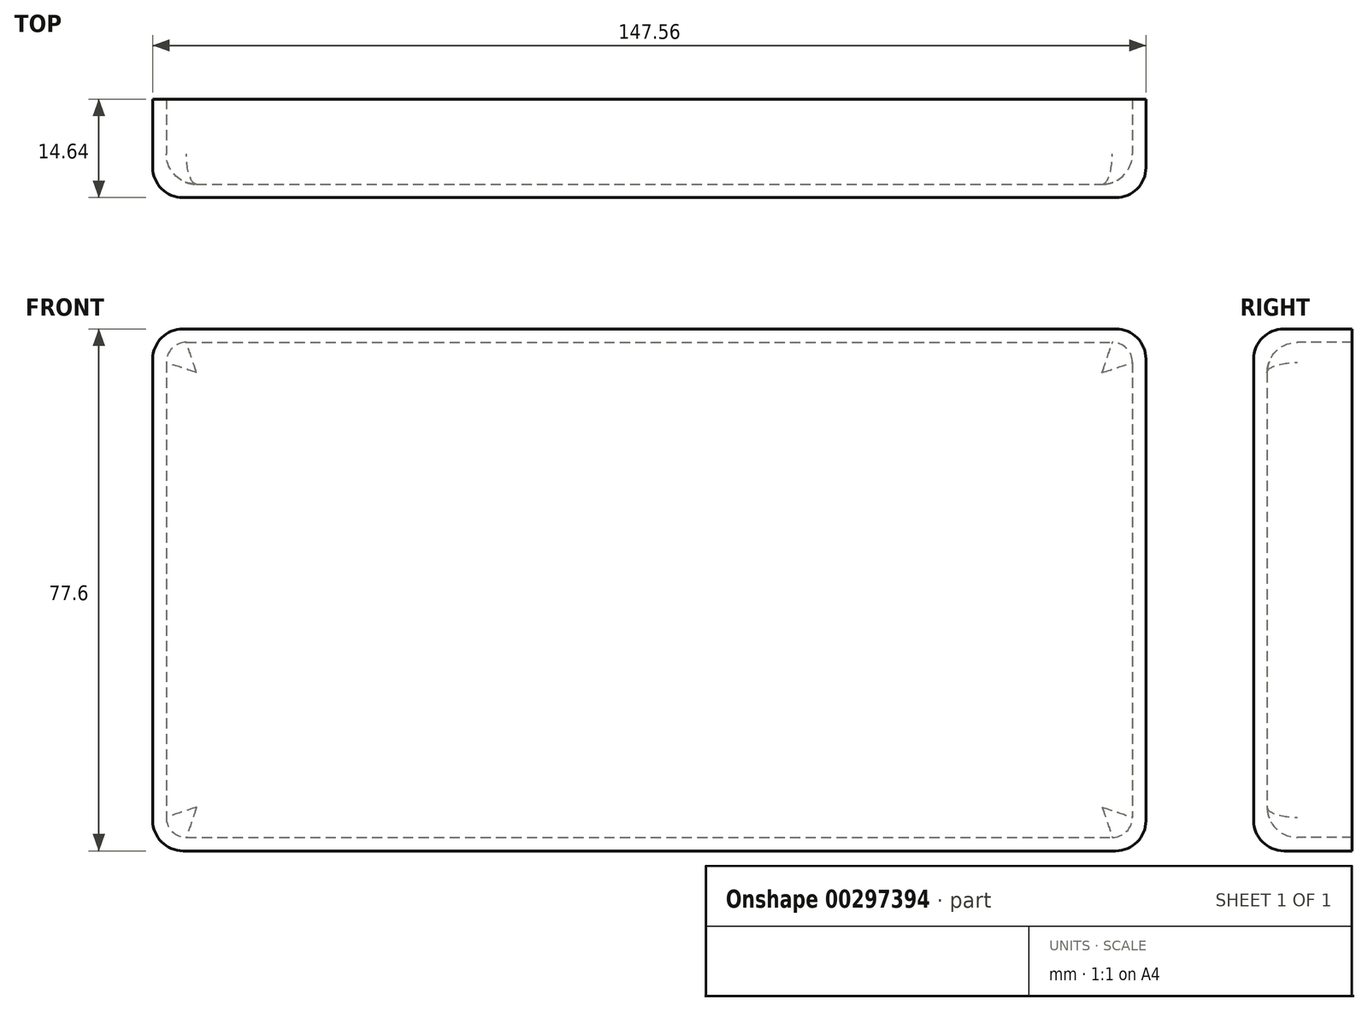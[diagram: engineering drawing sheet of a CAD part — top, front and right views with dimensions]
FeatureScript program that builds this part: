
annotation { "Feature Type Name" : "Feature", "Feature Type Description" : "" }
export const myFeature = defineFeature(function(context is Context, id is Id, definition is map)
    precondition{}
    {
        {
            var Q0;
            Q0=qCreatedBy(makeId("Front.planeOp"),FACE);
            var sketch = newSketch(context, id + "F0", { "sketchPlane" : qUnion([Q0])});
            skLineSegment(sketch, "E0.bottom", {"start": v(-72.06, 43.51) * mm, "end": v(71.5, 43.51) * mm});
            skLineSegment(sketch, "E0.top", {"start": v(-72.06, -30.09) * mm, "end": v(71.5, -30.09) * mm});
            skLineSegment(sketch, "E0.left", {"start": v(-72.06, 43.51) * mm, "end": v(-72.06, -30.09) * mm});
            skLineSegment(sketch, "E0.right", {"start": v(71.5, 43.51) * mm, "end": v(71.5, -30.09) * mm});
            skSolve(sketch);
        }
        {
            var Q0;
            Q0=makeQuery(id+"F0.imprint","IMPRINT",FACE,{"disambiguationData":[TD([[makeQuery(id+"F0.imprint","IMPRINT",EDGE,{"derivedFrom":sQuery(id+"F0.wireOp",EDGE,"E0.bottom")}),-1.0]])]});
            extrude(context, id + "F1", {"entities" : qUnion([Q0]), "oppositeDirection" : true, "depth" : 12.64 * mm});
        }
        {
            var Q0;
            Q0=makeQuery(id+"F1.opExtrude","CAP_FACE",FACE,{"disambiguationData":[OSD([sQuery(id+"F0.wireOp",EDGE,"E0.bottom"),sQuery(id+"F0.wireOp",EDGE,"E0.top"),sQuery(id+"F0.wireOp",EDGE,"E0.left"),sQuery(id+"F0.wireOp",EDGE,"E0.right")])],"isStart":false});
            shell(context, id + "F2", {"entities" : qUnion([Q0]), "thickness" : 2 * mm, "oppositeDirection" : true});
        }
        {
            var Q0;
            Q0=makeQuery(id+"F2.opShell","OFFSET_EDGE",EDGE,{"disambiguationData":[OSD([sQuery(id+"F0.wireOp",EDGE,"E0.top"),sQuery(id+"F0.wireOp",EDGE,"E0.right")])]});
            var Q1;
            Q1=makeQuery(id+"F2.opShell","OFFSET_EDGE",EDGE,{"disambiguationData":[OSD([sQuery(id+"F0.wireOp",EDGE,"E0.bottom"),sQuery(id+"F0.wireOp",EDGE,"E0.right")])]});
            var Q2;
            Q2=makeQuery(id+"F2.opShell","OFFSET_EDGE",EDGE,{"disambiguationData":[OSD([sQuery(id+"F0.wireOp",EDGE,"E0.bottom"),sQuery(id+"F0.wireOp",EDGE,"E0.left")])]});
            var Q3;
            Q3=makeQuery(id+"F2.opShell","OFFSET_EDGE",EDGE,{"disambiguationData":[OSD([sQuery(id+"F0.wireOp",EDGE,"E0.top"),sQuery(id+"F0.wireOp",EDGE,"E0.left")])]});
            fillet(context, id + "F3", {"entities" : qUnion([Q0, Q1, Q2, Q3]), "radius" : 3 * mm, "tangentPropagation" : true, "allowEdgeOverflow" : false});
        }
        {
            var Q0;
            {var subQ0=sQuery(id+"F0.wireOp",EDGE,"E0.right");Q0=makeQuery(id+"F2.opShell","OFFSET_EDGE",EDGE,{"disambiguationData":[OSD([subQ0]),TDD([makeQuery(id+"F1.opExtrude","CAP_EDGE",EDGE,{"disambiguationData":[OSD([subQ0])],"isStart":true})])]});}
            var Q1;
            Q1=makeQuery(id+"F2.opShell","OFFSET_FACE",FACE,{"disambiguationData":[OSD([sQuery(id+"F0.wireOp",EDGE,"E0.bottom"),sQuery(id+"F0.wireOp",EDGE,"E0.top"),sQuery(id+"F0.wireOp",EDGE,"E0.left"),sQuery(id+"F0.wireOp",EDGE,"E0.right")])]});
            var Q2;
            Q2=makeQuery(id+"F1.opExtrude","CAP_EDGE",EDGE,{"disambiguationData":[OSD([sQuery(id+"F0.wireOp",EDGE,"E0.bottom")])],"isStart":true});
            var Q3;
            Q3=makeQuery(id+"F1.opExtrude","CAP_EDGE",EDGE,{"disambiguationData":[OSD([sQuery(id+"F0.wireOp",EDGE,"E0.right")])],"isStart":true});
            var Q4;
            Q4=makeQuery(id+"F1.opExtrude","CAP_EDGE",EDGE,{"disambiguationData":[OSD([sQuery(id+"F0.wireOp",EDGE,"E0.top")])],"isStart":true});
            var Q5;
            Q5=makeQuery(id+"F1.opExtrude","CAP_EDGE",EDGE,{"disambiguationData":[OSD([sQuery(id+"F0.wireOp",EDGE,"E0.left")])],"isStart":true});
            var Q6;
            Q6=makeQuery(id+"F1.opExtrude","SWEPT_EDGE",EDGE,{"disambiguationData":[OSD([sQuery(id+"F0.wireOp",EDGE,"E0.bottom"),sQuery(id+"F0.wireOp",EDGE,"E0.left")])]});
            var Q7;
            Q7=makeQuery(id+"F1.opExtrude","SWEPT_EDGE",EDGE,{"disambiguationData":[OSD([sQuery(id+"F0.wireOp",EDGE,"E0.top"),sQuery(id+"F0.wireOp",EDGE,"E0.left")])]});
            var Q8;
            Q8=makeQuery(id+"F1.opExtrude","SWEPT_EDGE",EDGE,{"disambiguationData":[OSD([sQuery(id+"F0.wireOp",EDGE,"E0.top"),sQuery(id+"F0.wireOp",EDGE,"E0.right")])]});
            var Q9;
            Q9=makeQuery(id+"F1.opExtrude","SWEPT_EDGE",EDGE,{"disambiguationData":[OSD([sQuery(id+"F0.wireOp",EDGE,"E0.bottom"),sQuery(id+"F0.wireOp",EDGE,"E0.right")])]});
            fillet(context, id + "F4", {"entities" : qUnion([Q0, Q1, Q2, Q3, Q4, Q5, Q6, Q7, Q8, Q9]), "radius" : 4.5 * mm, "tangentPropagation" : true, "allowEdgeOverflow" : false});
        }
    });
